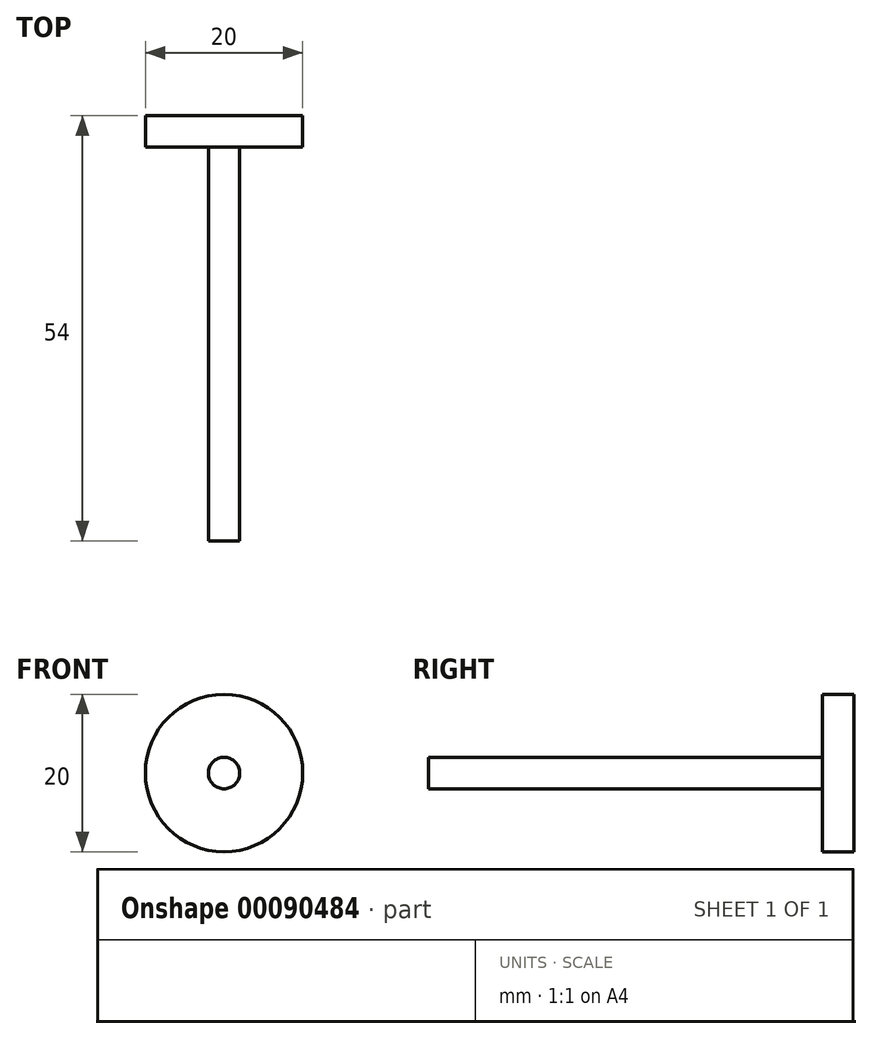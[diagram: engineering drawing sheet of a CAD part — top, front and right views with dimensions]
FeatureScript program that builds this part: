
annotation { "Feature Type Name" : "Feature", "Feature Type Description" : "" }
export const myFeature = defineFeature(function(context is Context, id is Id, definition is map)
    precondition{}
    {
        {
            var Q0;
            Q0=qCreatedBy(makeId("Front.planeOp"),FACE);
            var sketch = newSketch(context, id + "F0", { "sketchPlane" : qUnion([Q0])});
            skCircle(sketch, "E0", {"center": v(0, 0) * mm, "radius": 10 * mm});
            skSolve(sketch);
        }
        {
            var Q0;
            Q0 = qSketchRegion(id + "F0", true);
            extrude(context, id + "F1", {"entities" : qUnion([Q0]), "depth" : 4 * mm});
        }
        {
            var Q0;
            Q0=makeQuery(id+"F1.opExtrude","CAP_FACE",FACE,{"disambiguationData":[OSD([sQuery(id+"F0.wireOp",EDGE,"E0")])],"isStart":false});
            var sketch = newSketch(context, id + "F2", { "sketchPlane" : qUnion([Q0])});
            skCircle(sketch, "E1", {"center": v(0, 0) * mm, "radius": 2 * mm});
            skSolve(sketch);
        }
        {
            var Q0;
            Q0=makeQuery(id+"F2.imprint","IMPRINT",FACE,{"disambiguationData":[TD([[makeQuery(id+"F2.imprint","IMPRINT",EDGE,{"derivedFrom":sQuery(id+"F2.wireOp",EDGE,"E1")}),1.0]])]});
            extrude(context, id + "F3", {"entities" : qUnion([Q0]), "operationType" : NewBodyOperationType.ADD, "depth" : 50 * mm});
        }
    });
